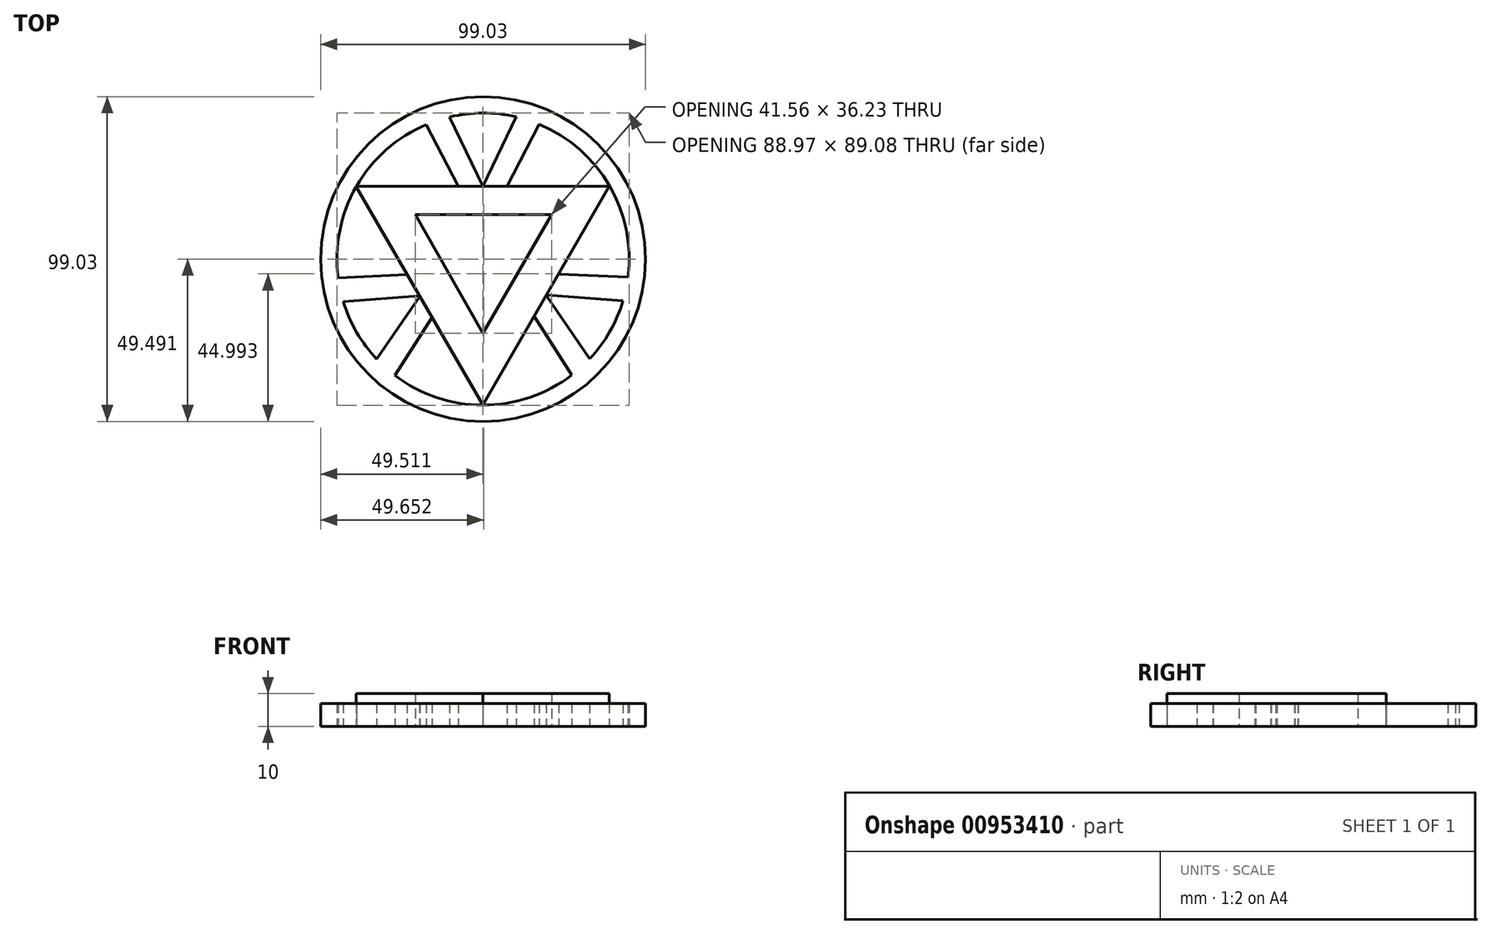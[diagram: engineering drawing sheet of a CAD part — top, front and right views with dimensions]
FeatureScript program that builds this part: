
annotation { "Feature Type Name" : "Feature", "Feature Type Description" : "" }
export const myFeature = defineFeature(function(context is Context, id is Id, definition is map)
    precondition{}
    {
        {
            var Q0;
            Q0=qCreatedBy(makeId("Top.planeOp"),FACE);
            var sketch = newSketch(context, id + "F0", { "sketchPlane" : qUnion([Q0])});
            skLineSegment(sketch, "E0", {"start": v(0, -44.7) * mm, "end": v(-38.63, 22.06) * mm});
            skLineSegment(sketch, "E1", {"start": v(-38.63, 22.06) * mm, "end": v(38.55, 22.06) * mm});
            skLineSegment(sketch, "E2", {"start": v(38.55, 22.06) * mm, "end": v(0, -44.7) * mm});
            skLineSegment(sketch, "E3", {"start": v(-17.26, 41) * mm, "end": v(-7.45, 22.06) * mm});
            skLineSegment(sketch, "E4", {"start": v(-10.22, 43.3) * mm, "end": v(-0.04, 22.06) * mm});
            skLineSegment(sketch, "E5.MirrorCS", {"start": v(10.22, 43.3) * mm, "end": v(0.04, 22.06) * mm});
            skLineSegment(sketch, "E6.MirrorCS", {"start": v(17.26, 41) * mm, "end": v(7.45, 22.06) * mm});
            skLineSegment(sketch, "E7.1.0", {"start": v(-42.61, -13.1) * mm, "end": v(-19.13, -11.29) * mm});
            skLineSegment(sketch, "E7.1.1", {"start": v(-44.14, -5.84) * mm, "end": v(-22.83, -4.88) * mm});
            skLineSegment(sketch, "E7.1.2", {"start": v(-32.4, -30.8) * mm, "end": v(-19.09, -11.36) * mm});
            skLineSegment(sketch, "E7.1.3", {"start": v(-26.88, -35.74) * mm, "end": v(-15.38, -17.77) * mm});
            skLineSegment(sketch, "E7.2.0", {"start": v(32.64, -30.65) * mm, "end": v(19.34, -11.21) * mm});
            skLineSegment(sketch, "E7.2.1", {"start": v(27.13, -35.6) * mm, "end": v(15.64, -17.63) * mm});
            skLineSegment(sketch, "E7.2.2", {"start": v(42.86, -12.95) * mm, "end": v(19.38, -11.14) * mm});
            skLineSegment(sketch, "E7.2.3", {"start": v(44.4, -5.7) * mm, "end": v(23.08, -4.73) * mm});
            skPoint(sketch, "E7.center", {"position": v(0.08, -0.15) * mm});
            skLineSegment(sketch, "E8", {"start": v(-20.56, 13.45) * mm, "end": v(21, 13.45) * mm});
            skLineSegment(sketch, "E9", {"start": v(21, 13.45) * mm, "end": v(0, -22.78) * mm});
            skLineSegment(sketch, "E10", {"start": v(0, -22.78) * mm, "end": v(-20.56, 13.45) * mm});
            skLineSegment(sketch, "E11", {"start": v(21, 13.45) * mm, "end": v(38.55, 22.06) * mm});
            skLineSegment(sketch, "E12", {"start": v(-20.56, 13.45) * mm, "end": v(-38.63, 22.06) * mm});
            skLineSegment(sketch, "E13", {"start": v(0, -22.78) * mm, "end": v(0, -44.7) * mm});
            skCircle(sketch, "E14", {"center": v(0.08, -0.15) * mm, "radius": 44.52 * mm});
            skCircle(sketch, "E15.0", {"center": v(0.08, -0.15) * mm, "radius": 49.52 * mm});
            skSolve(sketch);
        }
        {
            var Q0;
            Q0=makeQuery(id+"F0.imprint","IMPRINT",FACE,{"disambiguationData":[TD([[makeQuery(id+"F0.imprint","IMPRINT",EDGE,{"derivedFrom":sQuery(id+"F0.wireOp",EDGE,"E15.0")}),1.0]])]});
            var Q1;
            {var subQ0=sQuery(id+"F0.wireOp",EDGE,"E5.MirrorCS");var subQ1=sQuery(id+"F0.wireOp",EDGE,"E1");var subQ2=makeQuery(id+"F0.imprint","INTERSECT",VERTEX,{"derivedFrom":[subQ1,subQ0]});Q1=makeQuery(id+"F0.imprint","IMPRINT",FACE,{"disambiguationData":[TD([[makeQuery(id+"F0.imprint","IMPRINT",EDGE,{"disambiguationData":[TD([[subQ2,-1.0]])],"derivedFrom":subQ1}),1.0]])]});}
            var Q2;
            {var subQ0=sQuery(id+"F0.wireOp",EDGE,"E3");var subQ1=sQuery(id+"F0.wireOp",EDGE,"E1");var subQ2=makeQuery(id+"F0.imprint","INTERSECT",VERTEX,{"derivedFrom":[subQ1,subQ0]});Q2=makeQuery(id+"F0.imprint","IMPRINT",FACE,{"disambiguationData":[TD([[makeQuery(id+"F0.imprint","IMPRINT",EDGE,{"disambiguationData":[TD([[subQ2,-1.0]])],"derivedFrom":subQ1}),1.0]])]});}
            var Q3;
            {var subQ0=sQuery(id+"F0.wireOp",EDGE,"E7.2.2");var subQ1=sQuery(id+"F0.wireOp",EDGE,"E2");var subQ2=makeQuery(id+"F0.imprint","INTERSECT",VERTEX,{"derivedFrom":[subQ1,subQ0]});Q3=makeQuery(id+"F0.imprint","IMPRINT",FACE,{"disambiguationData":[TD([[makeQuery(id+"F0.imprint","IMPRINT",EDGE,{"disambiguationData":[TD([[subQ2,1.0]])],"derivedFrom":subQ1}),1.0]])]});}
            var Q4;
            {var subQ0=sQuery(id+"F0.wireOp",EDGE,"E7.2.0");var subQ1=sQuery(id+"F0.wireOp",EDGE,"E2");var subQ2=makeQuery(id+"F0.imprint","INTERSECT",VERTEX,{"derivedFrom":[subQ1,subQ0]});Q4=makeQuery(id+"F0.imprint","IMPRINT",FACE,{"disambiguationData":[TD([[makeQuery(id+"F0.imprint","IMPRINT",EDGE,{"disambiguationData":[TD([[subQ2,-1.0]])],"derivedFrom":subQ1}),1.0]])]});}
            var Q5;
            {var subQ0=sQuery(id+"F0.wireOp",EDGE,"E7.1.3");var subQ1=sQuery(id+"F0.wireOp",EDGE,"E0");var subQ2=makeQuery(id+"F0.imprint","INTERSECT",VERTEX,{"derivedFrom":[subQ1,subQ0]});Q5=makeQuery(id+"F0.imprint","IMPRINT",FACE,{"disambiguationData":[TD([[makeQuery(id+"F0.imprint","IMPRINT",EDGE,{"disambiguationData":[TD([[subQ2,-1.0]])],"derivedFrom":subQ1}),1.0]])]});}
            var Q6;
            {var subQ0=sQuery(id+"F0.wireOp",EDGE,"E7.1.0");var subQ1=sQuery(id+"F0.wireOp",EDGE,"E0");var subQ2=makeQuery(id+"F0.imprint","INTERSECT",VERTEX,{"derivedFrom":[subQ1,subQ0]});Q6=makeQuery(id+"F0.imprint","IMPRINT",FACE,{"disambiguationData":[TD([[makeQuery(id+"F0.imprint","IMPRINT",EDGE,{"disambiguationData":[TD([[subQ2,-1.0]])],"derivedFrom":subQ1}),1.0]])]});}
            extrude(context, id + "F1", {"entities" : qUnion([Q0, Q1, Q2, Q3, Q4, Q5, Q6]), "depth" : 7 * mm, "offsetDistance" : 25.4 * mm});
        }
        {
            var Q0;
            {var subQ9=sQuery(id+"F0.wireOp",EDGE,"E8");Q0=makeQuery(id+"F0.imprint","IMPRINT",FACE,{"disambiguationData":[TD([[makeQuery(id+"F0.imprint","IMPRINT",EDGE,{"derivedFrom":subQ9}),1.0]])]});}
            var Q1;
            {var subQ5=sQuery(id+"F0.wireOp",EDGE,"E9");Q1=makeQuery(id+"F0.imprint","IMPRINT",FACE,{"disambiguationData":[TD([[makeQuery(id+"F0.imprint","IMPRINT",EDGE,{"derivedFrom":subQ5}),1.0]])]});}
            var Q2;
            {var subQ4=sQuery(id+"F0.wireOp",EDGE,"E10");Q2=makeQuery(id+"F0.imprint","IMPRINT",FACE,{"disambiguationData":[TD([[makeQuery(id+"F0.imprint","IMPRINT",EDGE,{"derivedFrom":subQ4}),1.0]])]});}
            extrude(context, id + "F2", {"entities" : qUnion([Q0, Q1, Q2]), "depth" : 10 * mm, "offsetDistance" : 25 * mm});
        }
    });
